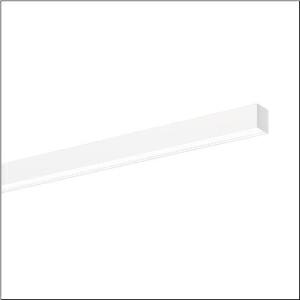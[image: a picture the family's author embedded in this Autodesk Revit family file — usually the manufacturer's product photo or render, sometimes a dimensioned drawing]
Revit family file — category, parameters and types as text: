
# Revit family: silica_r__21_51mx20db42wb_d1f2
name_source: partatom
category: Lighting Fixtures
units: mm (PartAtom-declared; Revit-internal decimal feet)

## family parameters
Cut with Voids When Loaded = No
Host = Face
Light Source = No
Part Type = Normal
Room Calculation Point = No
Round Connector Dimension = Use Diameter
Shared = No

## types (1)
- --- (1 x LED, 3000 lm, 19 W, 4000K)
    Apparent Load = 19 VA
    CIE Flux Codes = 48 79 96 100 100
    Color Rendering = 80
    Color Temperature = 4000K
    Default Elevation = 1800 mm
    Description = Silica® 21, office luminaire, primary optical cover: cover, of PMMA, opal, light emission: direct distribution, primary light characteristic: symmetric, installation type: surface-mounted, LED, rated luminous flux: 3.000lm, luminous efficacy: 158lm/W, light colour: 840, colour temperature: 4000K, with terminal, 3+2-pole, max. 2.5mm², mains connection: 220..240V, AC, 50/60Hz, rated input power: 19W, luminaire housing, of aluminium, traffic white (RAL 9016), length: 1.504mm, width: 53mm, height: 53mm, protection rating (complete): IP20, insulation class (complete): insulation class I (protective earthing), certification: CE, permissible operating ambient temperature: 0..+35°C, standard: EN 50419, packaging unit: 1 piece
    Height = 0 mm  [stored 0 ft]
    Lamp = 1 x LED
    Lamp Light Flux = 3000 lm
    Lamp Power = 19 W
    Lamp count = 1
    Length = 1504 mm
    Luminous efficacy = 158 lm/W
    Manufacturer = Siteco
    ModVariant = No
    Model = 51MX20DB42WB
    Mounting Place = Ceiling
    Mounting Type = Recessed
    Number of Poles = 1
    OnlyDefault = Yes
    Power Factor = 1
    Product Name = Silica® 21
    Product group = office luminaire | ceiling recessed
    ProductGroupID = 400
    Protection Class = Protection class I
    Protection Degree = IP 20
    RLX_Detail_Level = 1
    RLX_Emergency_Light_Flux = 0 lm
    RLX_Emergency_Type = 0
    RLX_Emergency_Type_DB = No
    RlxData = <blob elided: 23817 chars, md5=6f5ba325>
    Socket = socket
    Standby Power = 0 W
    System Light Flux = 3000 lm
    System Power = 19 W
    Type Comments = factory setting: luminous flux: 100 % | dim-lin: 254 | 218 mA
    Type Image = l_1335877.jpg
    URL = http://relux.com
    VarID = @adj_087257
    Voltage = 0 V
    Weight = 0.00 kg
    Width = 53 mm

note: [stored X ft] marks values corroborated as IEEE doubles in the binary element streams (Revit-internal decimal feet)

## geometry (parser evidence)
native form markers: Blend x4, Sweep x13
no freeform markers — native parametric forms only
